# Revit family: ASH_Contour21_S2122_BIM_GB
name_source: partatom
category: Plumbing Fixtures
revit_build: Autodesk Revit MEP 2014 (Build: 20130308_1515(x64)
units: mm (PartAtom-declared; Revit-internal decimal feet)

## types (1)
- S212201 - Contour 21 - 370mm - Handrinse Washbasin - 1 Taphole - No Overflow - No Chainstay Hole - Bottom Outlet
    Accessories = www.idealspec.co.uk
    AreaUnits = millimeters
    Assembly Code = C1030200
    AssetType = Fixed
    BIMObjectName = ASH_ArmitageShanks_WallHungHandRinseBasins_Contour21_S2122
    BarCode = 5017830379799
    Brand = Armitage Shanks
    CWFU = 0
    CodePerformance = Vitreous china to BS 3402
    Color = White
    ConnectionType = Plumbing
    Cost = 0 $
    Default Elevation = 850 mm  [stored 2.78871 ft]
    Description = Contour 21 37cm handrinse washbasin, 1 taphole, no overflow, no chainstay hole, bottom outlet
    DrainSize = 0 mm  [stored 0 ft]
    DurationUnit = year
    ECA = No
    ExpectedLife = 30
    Features = 37cm handrinse washbasin, 1 taphole, no overflow, no chainstay hole, bottom outlet
    Finish = White
    HWFU = 0
    Help = www.idealspec.co.uk/contact-us.html
    IfcExportAs = IfcSanitaryTerminalType
    IfcExportType = WASHHANDBASIN
    InstallationInstructions = www.idealspec.co.uk/resources.html
    LinearUnits = millimeters
    ManufacturerURL = www.idealspec.co.uk
    Material = Vitreous China
    Model = S212201
    NBSDescription = Wall hung hand rinse basins
    NBSReference = 45-35-70/368
    Name = WallHungHandRinseBasins_Contour21_S2122_ArmitageShanks
    NettWeight = 8.2 Kg
    NominalDepth = 305 mm
    NominalHeight = 165 mm
    NominalLength = 0 mm  [stored 0 ft]
    NominalWidth = 370 mm
    ProductInformation = www.idealspec.co.uk/assets/datasheet/S212201
    Shape = Sculptured
    Size = 305 x 165 x 370 mm
    Space = Internal
    URL = www.idealspec.co.uk
    Uniclass2015Code = Pr_40_20_96_95
    Uniclass2015Title = Wall-hung hand rinse basins
    Uniclass2015Version = Products v1.1
    Version = 1
    VolumeUnits = Litres
    WFU = 0
    WarrantyDescription = Manufacturers Warranty
    WarrantyDurationParts = 99
    WarrantyDurationUnit = year
    WashHandBasinMounting = Wall hung
    WashHandBasinType = Hand Rinse

note: [stored X ft] marks values corroborated as IEEE doubles in the binary element streams (Revit-internal decimal feet)

## geometry (parser evidence)
native form markers: Sweep x5
no freeform markers — native parametric forms only
